# Revit family: Ecowool Brownie Blanket (16kgm3)
name_source: partatom
category: Generic Models
units: mm (PartAtom-declared; Revit-internal decimal feet)

## family parameters
Can host rebar = No
Cut with Voids When Loaded = No
Host = Face
Part Type = Normal
Room Calculation Point = No
Round Connector Dimension = Use Diameter
Shared = No

## types (3) — shared parameters
Default Elevation = 1219 mm
Density = 16.00 kg/m³
Description = ECOWOOL Brownie blanket and slabs are resilient, non-combustible, glass mineral wool products, supplied at roofing and walling application for residential and commercial building
Finish = Brownie Blanket
Manufacturer = PGF Insulation Sdn. Bhd.
Thermal K value = 0.0366
Type of Insulation = Glass Mineral Wool Blanket
URL = www.ecowool.com.my

## per-type parameters (varying)
| type | Insulation Thickness | Thermal R value |
| EWBL 1.35 (50mm) | 50 mm  [stored 0.164042 ft] | 1.35 |
| EWBL 2.00 (75mm) | 75 mm | 2 |
| EWBL 2.70 (100mm) | 100 mm  [stored 0.328084 ft] | 2.7 |

note: [stored X ft] marks values corroborated as IEEE doubles in the binary element streams (Revit-internal decimal feet)

## geometry (parser evidence)
native form markers: Sweep x2
no freeform markers — native parametric forms only
